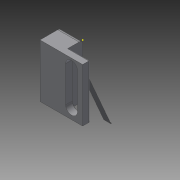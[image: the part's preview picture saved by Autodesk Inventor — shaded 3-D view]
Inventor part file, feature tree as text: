
AUTODESK INVENTOR PART (.ipt)
format: ipt  version: 2015 SP1 (Build 190203100, 203)  size: 152,576 bytes
history: native  units: mm
features: sketch x7, extrude x4, fillet x4, plane x2, sweep x1
ambient origin geometry x8: Origin, YZ Plane, XZ Plane, XY Plane, X Axis, Y Axis, Z Axis, Center Point
bodies: Solid1 (feature_tree)
feature tree (18):
  extrude  "Extrusion1"  Depth=30.0mm
  extrude  "Extrusion2"  Depth=4.0mm
  extrude  "Extrusion3"  Depth=12.0mm TaperAngle=0.0deg
  plane  "Work Plane1"
  sketch  "Sketch4"  dims[d13=0.025mm d14=2.0mm]
  sketch  "Sketch5"  dims[d15=0.0mm d16=0.0mm d17=4.0mm d18=0.0mm d19=0.1mm d20=2.0mm d21=0.5mm d22=0.2mm]
  sweep  "Sweep1"
  plane  "Work Plane2"
  extrude  "Extrusion4"  Depth=4.0mm TaperAngle=0.0deg
  fillet  "Fillet1"  Radius=0.1mm
  fillet  "Fillet2"  Radius=2.0mm
  fillet  "Fillet3"  Radius=0.5mm
  fillet  "Fillet4"  Radius=0.2mm
  sketch  "Sketch1"  dims[d0=12.0mm d1=30.0mm]
  sketch  "Sketch2"  dims[d2=12.0mm d3=0.0mm d4=4.0mm]
  sketch  "Sketch3"  dims[d5=12.0mm d6=0.0mm d7=12.0mm d8=0.0mm]
  sketch  "Sketch6"
  sketch  "Sketch7"
